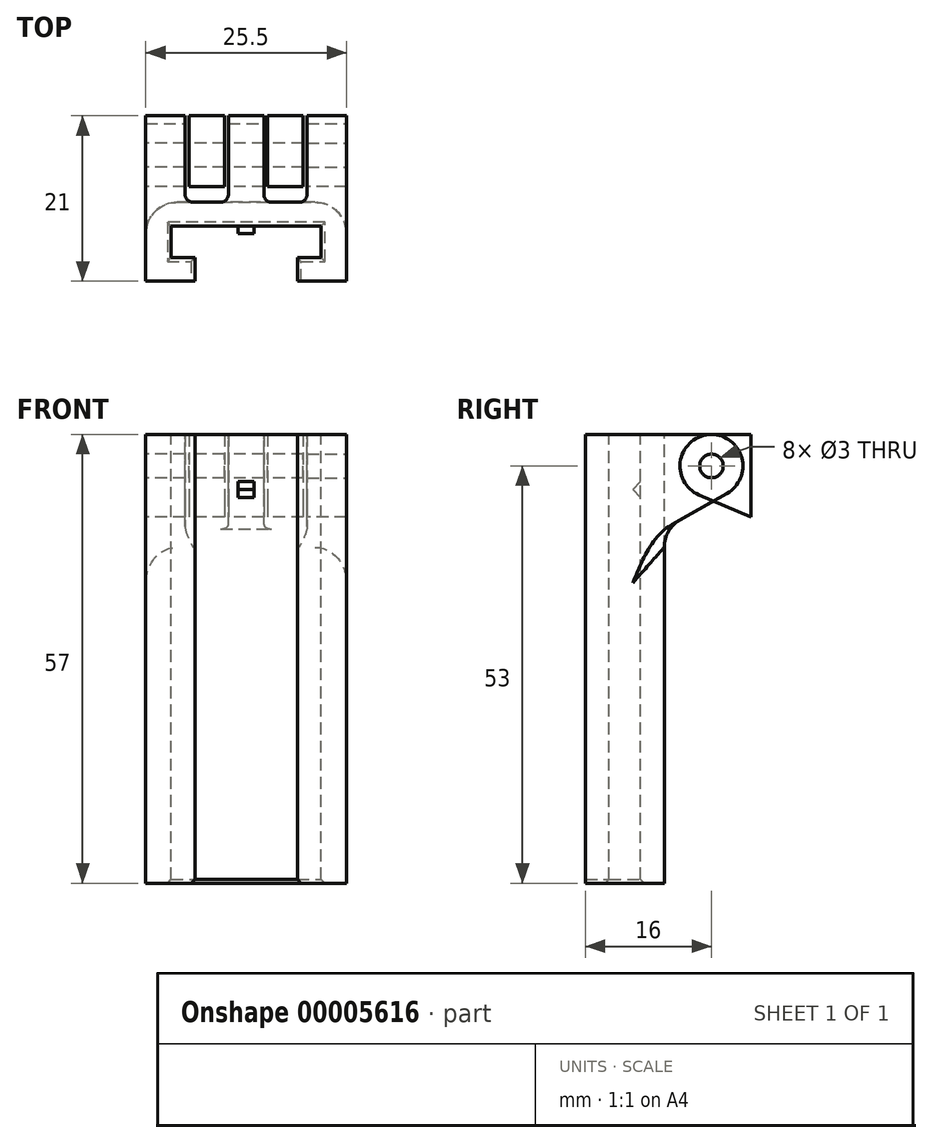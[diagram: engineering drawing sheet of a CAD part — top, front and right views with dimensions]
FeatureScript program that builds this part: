
annotation { "Feature Type Name" : "Feature", "Feature Type Description" : "" }
export const myFeature = defineFeature(function(context is Context, id is Id, definition is map)
    precondition{}
    {
        {
            var Q0;
            Q0=qCreatedBy(makeId("Top.planeOp"),FACE);
            var sketch = newSketch(context, id + "F0", { "sketchPlane" : qUnion([Q0])});
            skLineSegment(sketch, "E0.rect.bottom", {"start": v(12.75, -5) * mm, "end": v(-12.75, -5) * mm});
            skLineSegment(sketch, "E0.rect.top", {"start": v(12.75, 5) * mm, "end": v(-12.75, 5) * mm});
            skLineSegment(sketch, "E0.rect.left", {"start": v(12.75, -5) * mm, "end": v(12.75, 5) * mm});
            skLineSegment(sketch, "E0.rect.right", {"start": v(-12.75, -5) * mm, "end": v(-12.75, 5) * mm});
            skPoint(sketch, "E0.rect.middle", {"position": v(0, 0) * mm});
            skLineSegment(sketch, "E1.bottom", {"start": v(-6.5, -2) * mm, "end": v(6.5, -2) * mm});
            skLineSegment(sketch, "E1.top", {"start": v(-6.5, -5) * mm, "end": v(6.5, -5) * mm});
            skLineSegment(sketch, "E1.left", {"start": v(-6.5, -2) * mm, "end": v(-6.5, -5) * mm});
            skLineSegment(sketch, "E1.right", {"start": v(6.5, -2) * mm, "end": v(6.5, -5) * mm});
            skLineSegment(sketch, "E2.rect.bottom", {"start": v(9.5, -2) * mm, "end": v(-9.5, -2) * mm});
            skLineSegment(sketch, "E2.rect.top", {"start": v(9.5, 2) * mm, "end": v(-9.5, 2) * mm});
            skLineSegment(sketch, "E2.rect.left", {"start": v(9.5, -2) * mm, "end": v(9.5, 2) * mm});
            skLineSegment(sketch, "E2.rect.right", {"start": v(-9.5, -2) * mm, "end": v(-9.5, 2) * mm});
            skLineSegment(sketch, "E3.rect.bottom", {"start": v(2.75, 5) * mm, "end": v(-2.75, 5) * mm});
            skLineSegment(sketch, "E3.rect.top", {"start": v(2.75, 20.51) * mm, "end": v(-2.75, 20.51) * mm});
            skLineSegment(sketch, "E3.rect.left", {"start": v(2.75, 5) * mm, "end": v(2.75, 20.51) * mm});
            skLineSegment(sketch, "E3.rect.right", {"start": v(-2.75, 5) * mm, "end": v(-2.75, 20.51) * mm});
            skPoint(sketch, "E3.rect.middle", {"position": v(0, 12.76) * mm});
            skLineSegment(sketch, "E4", {"start": v(0, 28.5) * mm, "end": v(0, -14.85) * mm, "construction": true});
            skLineSegment(sketch, "E5.bottom", {"start": v(-12.75, 5) * mm, "end": v(-7.25, 5) * mm});
            skLineSegment(sketch, "E5.top", {"start": v(-12.75, 20.51) * mm, "end": v(-7.25, 20.51) * mm});
            skLineSegment(sketch, "E5.left", {"start": v(-12.75, 5) * mm, "end": v(-12.75, 20.51) * mm});
            skLineSegment(sketch, "E5.right", {"start": v(-7.25, 5) * mm, "end": v(-7.25, 20.51) * mm});
            skLineSegment(sketch, "E6.bottom", {"start": v(12.75, 5) * mm, "end": v(7.25, 5) * mm});
            skLineSegment(sketch, "E6.top", {"start": v(12.75, 20.51) * mm, "end": v(7.25, 20.51) * mm});
            skLineSegment(sketch, "E6.left", {"start": v(12.75, 5) * mm, "end": v(12.75, 20.51) * mm});
            skLineSegment(sketch, "E6.right", {"start": v(7.25, 5) * mm, "end": v(7.25, 20.51) * mm});
            skLineSegment(sketch, "E7", {"start": v(-7.25, 20.51) * mm, "end": v(-2.75, 5) * mm, "construction": true});
            skLineSegment(sketch, "E8", {"start": v(7.25, 20.51) * mm, "end": v(2.75, 5) * mm, "construction": true});
            skLineSegment(sketch, "E9.rect.bottom", {"start": v(-2.25, 5) * mm, "end": v(-7.75, 5) * mm});
            skLineSegment(sketch, "E9.rect.top", {"start": v(-2.25, 20.51) * mm, "end": v(-7.75, 20.51) * mm});
            skLineSegment(sketch, "E9.rect.left", {"start": v(-2.25, 5) * mm, "end": v(-2.25, 20.51) * mm});
            skLineSegment(sketch, "E9.rect.right", {"start": v(-7.75, 5) * mm, "end": v(-7.75, 20.51) * mm});
            skPoint(sketch, "E9.rect.middle", {"position": v(-5, 12.76) * mm});
            skLineSegment(sketch, "E10.rect.bottom", {"start": v(7.75, 5) * mm, "end": v(2.25, 5) * mm});
            skLineSegment(sketch, "E10.rect.top", {"start": v(7.75, 20.51) * mm, "end": v(2.25, 20.51) * mm});
            skLineSegment(sketch, "E10.rect.left", {"start": v(7.75, 5) * mm, "end": v(7.75, 20.51) * mm});
            skLineSegment(sketch, "E10.rect.right", {"start": v(2.25, 5) * mm, "end": v(2.25, 20.51) * mm});
            skPoint(sketch, "E10.rect.middle", {"position": v(5, 12.76) * mm});
            skSolve(sketch);
        }
        {
            var Q0;
            {var subQ15=sQuery(id+"F0.wireOp",EDGE,"E0.rect.left");Q0=makeQuery(id+"F0.imprint","IMPRINT",FACE,{"disambiguationData":[TD([[makeQuery(id+"F0.imprint","IMPRINT",EDGE,{"derivedFrom":subQ15}),1.0]])]});}
            extrude(context, id + "F1", {"entities" : qUnion([Q0]), "oppositeDirection" : true, "depth" : 57 * mm});
        }
        {
            var Q0;
            Q0=qCreatedBy(makeId("Right.planeOp"),FACE);
            var sketch = newSketch(context, id + "F2", { "sketchPlane" : qUnion([Q0])});
            skLineSegment(sketch, "E11.0.0", {"start": v(-5, 0) * mm, "end": v(5, 0) * mm, "construction": true});
            skLineSegment(sketch, "E12.0.3", {"start": v(2, -57) * mm, "end": v(2, 0) * mm, "construction": true});
            skLineSegment(sketch, "E13", {"start": v(2, -6) * mm, "end": v(1, -7) * mm});
            skLineSegment(sketch, "E14", {"start": v(1, -7) * mm, "end": v(2, -8) * mm});
            skLineSegment(sketch, "E15", {"start": v(2, -8) * mm, "end": v(2, -6) * mm});
            skLineSegment(sketch, "E16", {"start": v(12.97, -7.48) * mm, "end": v(5, -12) * mm});
            skLineSegment(sketch, "E17", {"start": v(5, 0) * mm, "end": v(11, 0) * mm});
            skLineSegment(sketch, "E18", {"start": v(5, -12) * mm, "end": v(5, 0) * mm});
            skCircle(sketch, "E19", {"center": v(11, -4) * mm, "radius": 4 * mm});
            skCircle(sketch, "E20", {"center": v(11, -4) * mm, "radius": 1.5 * mm});
            skLineSegment(sketch, "E21.0", {"start": v(5, -57) * mm, "end": v(5, 0) * mm, "construction": true});
            skLineSegment(sketch, "E22", {"start": v(11, -38.74) * mm, "end": v(11, 3.7) * mm, "construction": true});
            skLineSegment(sketch, "E23.bottom", {"start": v(11, 0) * mm, "end": v(16, 0) * mm});
            skLineSegment(sketch, "E23.top", {"start": v(11, -8.35) * mm, "end": v(16, -10.5) * mm});
            skLineSegment(sketch, "E23.left", {"start": v(11, 0) * mm, "end": v(11, -8.35) * mm});
            skLineSegment(sketch, "E23.right", {"start": v(16, 0) * mm, "end": v(16, -10.5) * mm});
            skCircle(sketch, "E24.cCircle", {"center": v(11, -4) * mm, "radius": 2.8 * mm, "construction": true});
            skLineSegment(sketch, "E24.0", {"start": v(9.38, -1.2) * mm, "end": v(12.62, -1.2) * mm});
            skLineSegment(sketch, "E24.1", {"start": v(12.62, -1.2) * mm, "end": v(14.23, -4) * mm});
            skLineSegment(sketch, "E24.2", {"start": v(14.23, -4) * mm, "end": v(12.62, -6.8) * mm});
            skLineSegment(sketch, "E24.3", {"start": v(12.62, -6.8) * mm, "end": v(9.38, -6.8) * mm});
            skLineSegment(sketch, "E24.4", {"start": v(9.38, -6.8) * mm, "end": v(7.77, -4) * mm});
            skLineSegment(sketch, "E24.5", {"start": v(7.77, -4) * mm, "end": v(9.38, -1.2) * mm});
            skPoint(sketch, "E24.0.midPoint", {"position": v(11, -1.2) * mm});
            skLineSegment(sketch, "E25", {"start": v(11, -8.35) * mm, "end": v(9.42, -7.68) * mm});
            skLineSegment(sketch, "E26", {"start": v(15, 0) * mm, "end": v(15, -4) * mm});
            skSolve(sketch);
        }
        {
            var Q0;
            {var subQ6=sQuery(id+"F2.wireOp",EDGE,"E24.1");Q0=makeQuery(id+"F2.imprint","IMPRINT",FACE,{"disambiguationData":[TD([[makeQuery(id+"F2.imprint","IMPRINT",EDGE,{"derivedFrom":subQ6}),1.0]])]});}
            var Q1;
            {var subQ0=sQuery(id+"F2.wireOp",EDGE,"E24.4");Q1=makeQuery(id+"F2.imprint","IMPRINT",FACE,{"disambiguationData":[TD([[makeQuery(id+"F2.imprint","IMPRINT",EDGE,{"derivedFrom":subQ0}),1.0]])]});}
            var Q2;
            {var subQ1=sQuery(id+"F2.wireOp",EDGE,"E19");var subQ5=sQuery(id+"F2.wireOp",EDGE,"E16");var subQ7=makeQuery(id+"F2.imprint","INTERSECT",VERTEX,{"derivedFrom":[subQ5,subQ1]});Q2=makeQuery(id+"F2.imprint","IMPRINT",FACE,{"disambiguationData":[TD([[makeQuery(id+"F2.imprint","IMPRINT",EDGE,{"disambiguationData":[TD([[subQ7,-1.0]])],"derivedFrom":subQ5}),-1.0]])]});}
            var Q3;
            {var subQ1=sQuery(id+"F2.wireOp",EDGE,"E24.4");Q3=makeQuery(id+"F2.imprint","IMPRINT",FACE,{"disambiguationData":[TD([[makeQuery(id+"F2.imprint","IMPRINT",EDGE,{"derivedFrom":subQ1}),-1.0]])]});}
            var Q4;
            {var subQ4=sQuery(id+"F2.wireOp",EDGE,"E24.1");Q4=makeQuery(id+"F2.imprint","IMPRINT",FACE,{"disambiguationData":[TD([[makeQuery(id+"F2.imprint","IMPRINT",EDGE,{"derivedFrom":subQ4}),-1.0]])]});}
            var Q5;
            {var subQ0=sQuery(id+"F2.wireOp",EDGE,"E25");Q5=makeQuery(id+"F2.imprint","IMPRINT",FACE,{"disambiguationData":[TD([[makeQuery(id+"F2.imprint","IMPRINT",EDGE,{"derivedFrom":subQ0}),-1.0]])]});}
            var Q6;
            {var subQ6=sQuery(id+"F2.wireOp",EDGE,"E17");Q6=makeQuery(id+"F2.imprint","IMPRINT",FACE,{"disambiguationData":[TD([[makeQuery(id+"F2.imprint","IMPRINT",EDGE,{"derivedFrom":subQ6}),-1.0]])]});}
            var Q7;
            Q7=makeQuery(id+"F1.opExtrude","SWEPT_FACE",FACE,{"disambiguationData":[OSD([sQuery(id+"F0.wireOp",EDGE,"E0.rect.top")])]});
            extrude(context, id + "F3", {"entities" : qUnion([Q0, Q1, Q2, Q3, Q4, Q5, Q6]), "operationType" : NewBodyOperationType.ADD, "endBound" : BoundingType.SYMMETRIC, "oppositeDirection" : true, "endBoundEntity" : qUnion([Q7]), "depth" : 25.5 * mm});
        }
        {
            var Q0;
            Q0=makeQuery(id+"F2.imprint","IMPRINT",FACE,{"disambiguationData":[TD([[makeQuery(id+"F2.imprint","IMPRINT",EDGE,{"derivedFrom":sQuery(id+"F2.wireOp",EDGE,"E13")}),1.0]])]});
            extrude(context, id + "F4", {"entities" : qUnion([Q0]), "operationType" : NewBodyOperationType.ADD, "endBound" : BoundingType.SYMMETRIC, "depth" : 2 * mm});
        }
        {
            var Q0;
            {var subQ1=sQuery(id+"F0.wireOp",EDGE,"E5.right");var subQ3=sQuery(id+"F0.wireOp",EDGE,"E3.rect.right");var subQ8=makeQuery(id+"F0.imprint","IMPRINT",EDGE,{"derivedFrom":subQ1});var subQ9=makeQuery(id+"F0.imprint","IMPRINT",EDGE,{"derivedFrom":subQ3});Q0=qUnion([makeQuery(id+"F0.imprint","IMPRINT",FACE,{"disambiguationData":[TD([[subQ9,1.0]])]}),makeQuery(id+"F0.imprint","IMPRINT",FACE,{"disambiguationData":[TD([[subQ9,-1.0]])]}),makeQuery(id+"F0.imprint","IMPRINT",FACE,{"disambiguationData":[TD([[subQ8,1.0]])]})]);}
            var Q1;
            {var subQ1=sQuery(id+"F0.wireOp",EDGE,"E6.right");var subQ3=sQuery(id+"F0.wireOp",EDGE,"E3.rect.left");var subQ8=makeQuery(id+"F0.imprint","IMPRINT",EDGE,{"derivedFrom":subQ1});var subQ9=makeQuery(id+"F0.imprint","IMPRINT",EDGE,{"derivedFrom":subQ3});Q1=qUnion([makeQuery(id+"F0.imprint","IMPRINT",FACE,{"disambiguationData":[TD([[subQ9,-1.0]])]}),makeQuery(id+"F0.imprint","IMPRINT",FACE,{"disambiguationData":[TD([[subQ9,1.0]])]}),makeQuery(id+"F0.imprint","IMPRINT",FACE,{"disambiguationData":[TD([[subQ8,-1.0]])]})]);}
            var Q2;
            {var subQ2=sQuery(id+"F0.wireOp",EDGE,"E5.right");Q2=makeQuery(id+"F0.imprint","IMPRINT",FACE,{"disambiguationData":[TD([[makeQuery(id+"F0.imprint","IMPRINT",EDGE,{"derivedFrom":subQ2}),1.0]])]});}
            var Q3;
            {var subQ2=sQuery(id+"F0.wireOp",EDGE,"E3.rect.right");Q3=makeQuery(id+"F0.imprint","IMPRINT",FACE,{"disambiguationData":[TD([[makeQuery(id+"F0.imprint","IMPRINT",EDGE,{"derivedFrom":subQ2}),-1.0]])]});}
            var Q4;
            {var subQ2=sQuery(id+"F0.wireOp",EDGE,"E3.rect.left");Q4=makeQuery(id+"F0.imprint","IMPRINT",FACE,{"disambiguationData":[TD([[makeQuery(id+"F0.imprint","IMPRINT",EDGE,{"derivedFrom":subQ2}),1.0]])]});}
            var Q5;
            {var subQ2=sQuery(id+"F0.wireOp",EDGE,"E6.right");Q5=makeQuery(id+"F0.imprint","IMPRINT",FACE,{"disambiguationData":[TD([[makeQuery(id+"F0.imprint","IMPRINT",EDGE,{"derivedFrom":subQ2}),-1.0]])]});}
            extrude(context, id + "F5", {"entities" : qUnion([Q0, Q1, Q2, Q3, Q4, Q5]), "operationType" : NewBodyOperationType.REMOVE, "oppositeDirection" : true, "depth" : 25 * mm});
        }
        {
            var Q0;
            Q0=makeQuery(id+"F1.opExtrude","SWEPT_EDGE",EDGE,{"disambiguationData":[OSD([sQuery(id+"F0.wireOp",EDGE,"E0.rect.right"),sQuery(id+"F0.wireOp",EDGE,"E5.bottom"),sQuery(id+"F0.wireOp",EDGE,"E5.left")])]});
            var Q1;
            Q1=makeQuery(id+"F1.opExtrude","SWEPT_EDGE",EDGE,{"disambiguationData":[OSD([sQuery(id+"F0.wireOp",EDGE,"E0.rect.left"),sQuery(id+"F0.wireOp",EDGE,"E6.bottom"),sQuery(id+"F0.wireOp",EDGE,"E6.left")])]});
            fillet(context, id + "F6", {"entities" : qUnion([Q0, Q1]), "radius" : 4 * mm, "tangentPropagation" : true, "allowEdgeOverflow" : false});
        }
        {
            var Q0;
            {var subQ1=sQuery(id+"F2.wireOp",EDGE,"E24.4");Q0=makeQuery(id+"F2.imprint","IMPRINT",FACE,{"disambiguationData":[TD([[makeQuery(id+"F2.imprint","IMPRINT",EDGE,{"derivedFrom":subQ1}),-1.0]])]});}
            var Q1;
            {var subQ4=sQuery(id+"F2.wireOp",EDGE,"E24.1");Q1=makeQuery(id+"F2.imprint","IMPRINT",FACE,{"disambiguationData":[TD([[makeQuery(id+"F2.imprint","IMPRINT",EDGE,{"derivedFrom":subQ4}),-1.0]])]});}
            var Q2;
            {var subQ0=sQuery(id+"F2.wireOp",EDGE,"E26");Q2=makeQuery(id+"F2.imprint","IMPRINT",FACE,{"disambiguationData":[TD([[makeQuery(id+"F2.imprint","IMPRINT",EDGE,{"derivedFrom":subQ0}),-1.0]])]});}
            var Q3;
            {var subQ1=sQuery(id+"F2.wireOp",EDGE,"E19");var subQ5=sQuery(id+"F2.wireOp",EDGE,"E16");var subQ7=makeQuery(id+"F2.imprint","INTERSECT",VERTEX,{"derivedFrom":[subQ5,subQ1]});Q3=makeQuery(id+"F2.imprint","IMPRINT",FACE,{"disambiguationData":[TD([[makeQuery(id+"F2.imprint","IMPRINT",EDGE,{"disambiguationData":[TD([[subQ7,-1.0]])],"derivedFrom":subQ5}),-1.0]])]});}
            var Q4;
            {var subQ6=sQuery(id+"F2.wireOp",EDGE,"E24.1");Q4=makeQuery(id+"F2.imprint","IMPRINT",FACE,{"disambiguationData":[TD([[makeQuery(id+"F2.imprint","IMPRINT",EDGE,{"derivedFrom":subQ6}),1.0]])]});}
            var Q5;
            {var subQ0=sQuery(id+"F2.wireOp",EDGE,"E24.4");Q5=makeQuery(id+"F2.imprint","IMPRINT",FACE,{"disambiguationData":[TD([[makeQuery(id+"F2.imprint","IMPRINT",EDGE,{"derivedFrom":subQ0}),1.0]])]});}
            var Q6;
            {var subQ0=sQuery(id+"F2.wireOp",EDGE,"E25");Q6=makeQuery(id+"F2.imprint","IMPRINT",FACE,{"disambiguationData":[TD([[makeQuery(id+"F2.imprint","IMPRINT",EDGE,{"derivedFrom":subQ0}),-1.0]])]});}
            var Q7;
            {var subQ1=sQuery(id+"F2.wireOp",EDGE,"E23.right");Q7=makeQuery(id+"F2.imprint","IMPRINT",FACE,{"disambiguationData":[TD([[makeQuery(id+"F2.imprint","IMPRINT",EDGE,{"derivedFrom":subQ1}),-1.0]])]});}
            extrude(context, id + "F7", {"entities" : qUnion([Q0, Q1, Q2, Q3, Q4, Q5, Q6, Q7]), "endBound" : BoundingType.SYMMETRIC, "depth" : 25.5 * mm});
        }
        {
            var Q0;
            Q0=makeQuery(id+"F0.imprint","IMPRINT",FACE,{"disambiguationData":[TD([[makeQuery(id+"F0.imprint","IMPRINT",EDGE,{"derivedFrom":sQuery(id+"F0.wireOp",EDGE,"E3.rect.bottom")}),-1.0]])]});
            var Q1;
            Q1=makeQuery(id+"F0.imprint","IMPRINT",FACE,{"disambiguationData":[TD([[makeQuery(id+"F0.imprint","IMPRINT",EDGE,{"derivedFrom":sQuery(id+"F0.wireOp",EDGE,"E5.bottom")}),1.0]])]});
            var Q2;
            Q2=makeQuery(id+"F0.imprint","IMPRINT",FACE,{"disambiguationData":[TD([[makeQuery(id+"F0.imprint","IMPRINT",EDGE,{"derivedFrom":sQuery(id+"F0.wireOp",EDGE,"E6.bottom")}),-1.0]])]});
            var Q3;
            {var subQ2=sQuery(id+"F0.wireOp",EDGE,"E5.right");Q3=makeQuery(id+"F0.imprint","IMPRINT",FACE,{"disambiguationData":[TD([[makeQuery(id+"F0.imprint","IMPRINT",EDGE,{"derivedFrom":subQ2}),1.0]])]});}
            var Q4;
            {var subQ2=sQuery(id+"F0.wireOp",EDGE,"E3.rect.right");Q4=makeQuery(id+"F0.imprint","IMPRINT",FACE,{"disambiguationData":[TD([[makeQuery(id+"F0.imprint","IMPRINT",EDGE,{"derivedFrom":subQ2}),-1.0]])]});}
            var Q5;
            {var subQ2=sQuery(id+"F0.wireOp",EDGE,"E3.rect.left");Q5=makeQuery(id+"F0.imprint","IMPRINT",FACE,{"disambiguationData":[TD([[makeQuery(id+"F0.imprint","IMPRINT",EDGE,{"derivedFrom":subQ2}),1.0]])]});}
            var Q6;
            {var subQ2=sQuery(id+"F0.wireOp",EDGE,"E6.right");Q6=makeQuery(id+"F0.imprint","IMPRINT",FACE,{"disambiguationData":[TD([[makeQuery(id+"F0.imprint","IMPRINT",EDGE,{"derivedFrom":subQ2}),-1.0]])]});}
            extrude(context, id + "F8", {"entities" : qUnion([Q0, Q1, Q2, Q3, Q4, Q5, Q6]), "operationType" : NewBodyOperationType.REMOVE, "oppositeDirection" : true, "depth" : 25 * mm});
        }
        {
            var Q0;
            {var subQ0=sQuery(id+"F0.wireOp",EDGE,"E0.rect.right");var subQ1=sQuery(id+"F0.wireOp",EDGE,"E5.bottom");var subQ2=sQuery(id+"F2.wireOp",EDGE,"E16");Q0=makeQuery(id+"F6.opFillet","BLEND_EDGE",EDGE,{"blendedFrom":[makeQuery(id+"F1.opExtrude","SWEPT_EDGE",EDGE,{"disambiguationData":[OSD([subQ0,subQ1,sQuery(id+"F0.wireOp",EDGE,"E5.left")])]}),makeQuery(id+"F5.boolean.opBoolean","SPLIT",FACE,{"disambiguationData":[TD([makeQuery(id+"F1.opExtrude","SWEPT_FACE",FACE,{"disambiguationData":[OSD([subQ0])]})])],"derivedFrom":makeQuery(id+"F3.opExtrude","SWEPT_FACE",FACE,{"disambiguationData":[OSD([subQ2])]})})],"blendedInto":[makeQuery(id+"F5.boolean.opBoolean","SPLIT",FACE,{"disambiguationData":[TD([makeQuery(id+"F1.opExtrude","SWEPT_FACE",FACE,{"disambiguationData":[OSD([subQ0])]})])],"derivedFrom":makeQuery(id+"F3.opExtrude","SWEPT_FACE",FACE,{"disambiguationData":[OSD([subQ2])]})})]});}
            var Q1;
            {var subQ0=sQuery(id+"F2.wireOp",EDGE,"E16");var subQ1=sQuery(id+"F2.wireOp",EDGE,"E18");Q1=makeQuery(id+"F5.boolean.opBoolean","SPLIT",EDGE,{"disambiguationData":[TD([makeQuery(id+"F1.opExtrude","SWEPT_FACE",FACE,{"disambiguationData":[OSD([sQuery(id+"F0.wireOp",EDGE,"E0.rect.right")])]})])],"derivedFrom":makeQuery(id+"F3.opExtrude","SWEPT_EDGE",EDGE,{"disambiguationData":[OSD([subQ0,subQ1])]})});}
            var Q2;
            {var subQ0=sQuery(id+"F2.wireOp",EDGE,"E16");Q2=makeQuery(id+"F5.boolean.opBoolean","SPLIT",EDGE,{"disambiguationData":[TD([makeQuery(id+"F5.opExtrude","SWEPT_FACE",FACE,{"disambiguationData":[OSD([sQuery(id+"F0.wireOp",EDGE,"E9.rect.left")])]})])],"derivedFrom":makeQuery(id+"F3.opExtrude","SWEPT_EDGE",EDGE,{"disambiguationData":[OSD([subQ0,sQuery(id+"F2.wireOp",EDGE,"E18")])]})});}
            var Q3;
            {var subQ0=sQuery(id+"F0.wireOp",EDGE,"E0.rect.left");var subQ1=sQuery(id+"F0.wireOp",EDGE,"E6.bottom");var subQ2=sQuery(id+"F2.wireOp",EDGE,"E16");Q3=makeQuery(id+"F6.opFillet","BLEND_EDGE",EDGE,{"blendedFrom":[makeQuery(id+"F1.opExtrude","SWEPT_EDGE",EDGE,{"disambiguationData":[OSD([subQ0,subQ1,sQuery(id+"F0.wireOp",EDGE,"E6.left")])]}),makeQuery(id+"F5.boolean.opBoolean","SPLIT",FACE,{"disambiguationData":[TD([makeQuery(id+"F1.opExtrude","SWEPT_FACE",FACE,{"disambiguationData":[OSD([subQ0])]})])],"derivedFrom":makeQuery(id+"F3.opExtrude","SWEPT_FACE",FACE,{"disambiguationData":[OSD([subQ2])]})})],"blendedInto":[makeQuery(id+"F5.boolean.opBoolean","SPLIT",FACE,{"disambiguationData":[TD([makeQuery(id+"F1.opExtrude","SWEPT_FACE",FACE,{"disambiguationData":[OSD([subQ0])]})])],"derivedFrom":makeQuery(id+"F3.opExtrude","SWEPT_FACE",FACE,{"disambiguationData":[OSD([subQ2])]})})]});}
            var Q4;
            {var subQ0=sQuery(id+"F2.wireOp",EDGE,"E16");var subQ1=sQuery(id+"F2.wireOp",EDGE,"E18");Q4=makeQuery(id+"F5.boolean.opBoolean","SPLIT",EDGE,{"disambiguationData":[TD([makeQuery(id+"F1.opExtrude","SWEPT_FACE",FACE,{"disambiguationData":[OSD([sQuery(id+"F0.wireOp",EDGE,"E0.rect.left")])]})])],"derivedFrom":makeQuery(id+"F3.opExtrude","SWEPT_EDGE",EDGE,{"disambiguationData":[OSD([subQ0,subQ1])]})});}
            fillet(context, id + "F9", {"entities" : qUnion([Q0, Q1, Q2, Q3, Q4]), "radius" : 4 * mm, "tangentPropagation" : true, "allowEdgeOverflow" : false});
        }
        {
            var Q0;
            Q0=makeQuery(id+"F5.boolean.opBoolean","COPY",EDGE,{"derivedFrom":makeQuery(id+"F5.opExtrude","SWEPT_EDGE",EDGE,{"disambiguationData":[OSD([sQuery(id+"F0.wireOp",EDGE,"E5.bottom"),sQuery(id+"F0.wireOp",EDGE,"E9.rect.bottom"),sQuery(id+"F0.wireOp",EDGE,"E9.rect.right")])]})});
            var Q1;
            Q1=makeQuery(id+"F5.boolean.opBoolean","COPY",EDGE,{"derivedFrom":makeQuery(id+"F5.opExtrude","SWEPT_EDGE",EDGE,{"disambiguationData":[OSD([sQuery(id+"F0.wireOp",EDGE,"E3.rect.bottom"),sQuery(id+"F0.wireOp",EDGE,"E10.rect.bottom"),sQuery(id+"F0.wireOp",EDGE,"E10.rect.right")])]})});
            var Q2;
            Q2=makeQuery(id+"F5.boolean.opBoolean","COPY",EDGE,{"derivedFrom":makeQuery(id+"F5.opExtrude","SWEPT_EDGE",EDGE,{"disambiguationData":[OSD([sQuery(id+"F0.wireOp",EDGE,"E6.bottom"),sQuery(id+"F0.wireOp",EDGE,"E10.rect.bottom"),sQuery(id+"F0.wireOp",EDGE,"E10.rect.left")])]})});
            var Q3;
            Q3=makeQuery(id+"F5.boolean.opBoolean","COPY",EDGE,{"derivedFrom":makeQuery(id+"F5.opExtrude","SWEPT_EDGE",EDGE,{"disambiguationData":[OSD([sQuery(id+"F0.wireOp",EDGE,"E3.rect.bottom"),sQuery(id+"F0.wireOp",EDGE,"E9.rect.bottom"),sQuery(id+"F0.wireOp",EDGE,"E9.rect.left")])]})});
            fillet(context, id + "F10", {"entities" : qUnion([Q0, Q1, Q2, Q3]), "radius" : 1 * mm, "tangentPropagation" : true, "allowEdgeOverflow" : false});
        }
        {
            var Q0;
            Q0=makeQuery(id+"F1.opExtrude","CAP_EDGE",EDGE,{"disambiguationData":[OSD([sQuery(id+"F0.wireOp",EDGE,"E3.rect.bottom"),sQuery(id+"F0.wireOp",EDGE,"E5.bottom"),sQuery(id+"F0.wireOp",EDGE,"E6.bottom"),sQuery(id+"F0.wireOp",EDGE,"E9.rect.bottom"),sQuery(id+"F0.wireOp",EDGE,"E10.rect.bottom")])],"isStart":false});
            var Q1;
            Q1=makeQuery(id+"F1.opExtrude","CAP_EDGE",EDGE,{"disambiguationData":[OSD([sQuery(id+"F0.wireOp",EDGE,"E2.rect.top")])],"isStart":false});
            var Q2;
            Q2=makeQuery(id+"F1.opExtrude","CAP_EDGE",EDGE,{"disambiguationData":[OSD([sQuery(id+"F0.wireOp",EDGE,"E2.rect.right")])],"isStart":false});
            var Q3;
            Q3=makeQuery(id+"F1.opExtrude","CAP_EDGE",EDGE,{"disambiguationData":[OSD([sQuery(id+"F0.wireOp",EDGE,"E1.left")])],"isStart":false});
            var Q4;
            Q4=makeQuery(id+"F1.opExtrude","CAP_EDGE",EDGE,{"disambiguationData":[OSD([sQuery(id+"F0.wireOp",EDGE,"E1.right")])],"isStart":false});
            var Q5;
            {var subQ0=sQuery(id+"F0.wireOp",EDGE,"E2.rect.bottom");Q5=makeQuery(id+"F1.opExtrude","CAP_EDGE",EDGE,{"disambiguationData":[OSD([subQ0]),TDD([makeQuery(id+"F0.imprint","IMPRINT",EDGE,{"disambiguationData":[TD([[makeQuery(id+"F0.imprint","INTERSECT",VERTEX,{"derivedFrom":[sQuery(id+"F0.wireOp",EDGE,"E1.right"),subQ0]}),1.0]])],"derivedFrom":subQ0})])],"isStart":false});}
            var Q6;
            Q6=makeQuery(id+"F1.opExtrude","CAP_EDGE",EDGE,{"disambiguationData":[OSD([sQuery(id+"F0.wireOp",EDGE,"E2.rect.left")])],"isStart":false});
            var Q7;
            {var subQ0=sQuery(id+"F0.wireOp",EDGE,"E2.rect.bottom");Q7=makeQuery(id+"F1.opExtrude","CAP_EDGE",EDGE,{"disambiguationData":[OSD([subQ0]),TDD([makeQuery(id+"F0.imprint","IMPRINT",EDGE,{"disambiguationData":[TD([[makeQuery(id+"F0.imprint","INTERSECT",VERTEX,{"derivedFrom":[sQuery(id+"F0.wireOp",EDGE,"E1.left"),subQ0]}),-1.0]])],"derivedFrom":subQ0})])],"isStart":false});}
            chamfer(context, id + "F11", {"entities" : qUnion([Q0, Q1, Q2, Q3, Q4, Q5, Q6, Q7]), "width" : .5 * mm, "tangentPropagation" : true});
        }
    });
